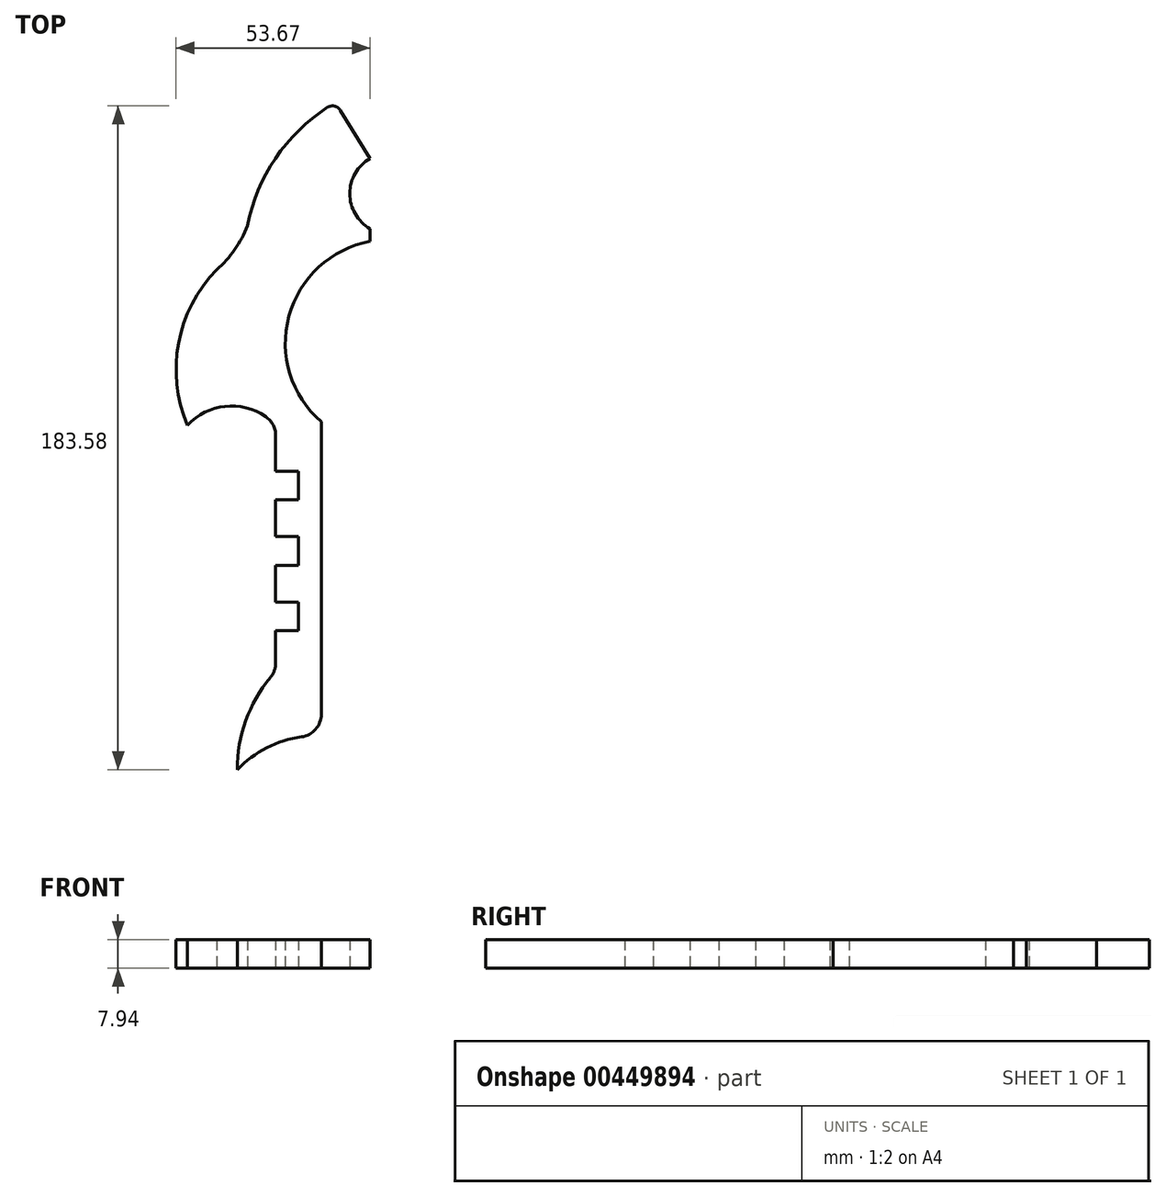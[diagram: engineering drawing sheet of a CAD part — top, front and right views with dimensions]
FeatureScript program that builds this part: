
annotation { "Feature Type Name" : "Feature", "Feature Type Description" : "" }
export const myFeature = defineFeature(function(context is Context, id is Id, definition is map)
    precondition{}
    {
        {
            var Q0;
            Q0=qCreatedBy(makeId("Top.planeOp"),FACE);
            var sketch = newSketch(context, id + "F0", { "sketchPlane" : qUnion([Q0])});
            skPoint(sketch, "E0.middle", {"position": v(0, -29.8) * mm});
            skLineSegment(sketch, "E1.left", {"start": v(-17.62, 5.43) * mm, "end": v(-17.62, -65.05) * mm});
            skLineSegment(sketch, "E2", {"start": v(-17.62, -65.05) * mm, "end": v(-17.62, -75.42) * mm});
            skArc(sketch, "E3", {"start": v(-23.09, -81.71) * mm, "mid": v(-32.73, -84.75) * mm, "end": v(-40.86, -90.77) * mm});
            skArc(sketch, "E4", {"start": v(-31.7, -65.27) * mm, "mid": v(-38.5, -77.22) * mm, "end": v(-40.86, -90.77) * mm});
            skPoint(sketch, "E4.startSnap0", {"position": v(-30.24, -83.62) * mm});
            skLineSegment(sketch, "E5", {"start": v(-30.24, -61.22) * mm, "end": v(-30.24, -52.32) * mm});
            skLineSegment(sketch, "E6", {"start": v(-30.24, -52.32) * mm, "end": v(-23.89, -52.32) * mm});
            skLineSegment(sketch, "E7", {"start": v(-23.89, -52.32) * mm, "end": v(-23.89, -44.39) * mm});
            skLineSegment(sketch, "E8", {"start": v(-23.89, -44.39) * mm, "end": v(-30.24, -44.39) * mm});
            skLineSegment(sketch, "E9", {"start": v(-30.24, -44.39) * mm, "end": v(-30.24, -34.23) * mm});
            skLineSegment(sketch, "E10", {"start": v(-30.24, -34.23) * mm, "end": v(-23.89, -34.23) * mm});
            skLineSegment(sketch, "E11", {"start": v(-23.89, -34.23) * mm, "end": v(-23.89, -26.29) * mm});
            skLineSegment(sketch, "E12", {"start": v(-23.89, -26.29) * mm, "end": v(-30.24, -26.29) * mm});
            skLineSegment(sketch, "E13", {"start": v(-30.24, -26.29) * mm, "end": v(-30.24, -16.13) * mm});
            skLineSegment(sketch, "E14", {"start": v(-30.24, -16.13) * mm, "end": v(-23.89, -16.13) * mm});
            skLineSegment(sketch, "E15", {"start": v(-23.89, -16.13) * mm, "end": v(-23.89, -8.2) * mm});
            skLineSegment(sketch, "E16", {"start": v(-23.89, -8.2) * mm, "end": v(-30.24, -8.2) * mm});
            skLineSegment(sketch, "E17", {"start": v(-30.24, -8.2) * mm, "end": v(-30.24, 1.63) * mm});
            skArc(sketch, "E18", {"start": v(-33.01, 6.88) * mm, "mid": v(-44.27, 9.7) * mm, "end": v(-54.66, 4.5) * mm});
            skArc(sketch, "E19", {"start": v(-46.54, 47.48) * mm, "mid": v(-57.1, 27.22) * mm, "end": v(-54.66, 4.5) * mm});
            skArc(sketch, "E20", {"start": v(-46.54, 47.48) * mm, "mid": v(-41.57, 53.08) * mm, "end": v(-38.02, 59.66) * mm});
            skArc(sketch, "E21", {"start": v(-15.89, 92.4) * mm, "mid": v(-30.3, 78.29) * mm, "end": v(-38.02, 59.66) * mm});
            skLineSegment(sketch, "E22", {"start": v(-12.35, 91.6) * mm, "end": v(-4.12, 78.3) * mm});
            skArc(sketch, "E23", {"start": v(-4.12, 78.3) * mm, "mid": v(-9.74, 68.56) * mm, "end": v(-4.12, 58.83) * mm});
            skLineSegment(sketch, "E24", {"start": v(-4.12, 58.83) * mm, "end": v(-4.12, 55.33) * mm});
            skArc(sketch, "E25", {"start": v(-4.12, 55.33) * mm, "mid": v(-26.57, 34.63) * mm, "end": v(-17.62, 5.43) * mm});
            skPoint(sketch, "E26.visualSharp", {"position": v(-17.62, -81.44) * mm});
            skArc(sketch, "E26.filletArc", {"start": v(-23.09, -81.71) * mm, "mid": v(-19.18, -79.6) * mm, "end": v(-17.62, -75.42) * mm});
            skPoint(sketch, "E27.visualSharp", {"position": v(-30.24, -63.6) * mm});
            skArc(sketch, "E27.filletArc", {"start": v(-31.7, -65.27) * mm, "mid": v(-30.61, -63.37) * mm, "end": v(-30.24, -61.22) * mm});
            skPoint(sketch, "E28.visualSharp", {"position": v(-30.24, 4.5) * mm});
            skArc(sketch, "E28.filletArc", {"start": v(-30.24, 1.63) * mm, "mid": v(-30.97, 4.6) * mm, "end": v(-33.01, 6.88) * mm});
            skPoint(sketch, "E29.visualSharp", {"position": v(-13.68, 93.75) * mm});
            skArc(sketch, "E29.filletArc", {"start": v(-12.35, 91.6) * mm, "mid": v(-13.95, 92.75) * mm, "end": v(-15.89, 92.4) * mm});
            skSolve(sketch);
        }
        {
            var Q0;
            Q0 = qSketchRegion(id + "F0", true);
            extrude(context, id + "F1", {"entities" : qUnion([Q0]), "depth" : 7.94 * mm});
        }
    });
